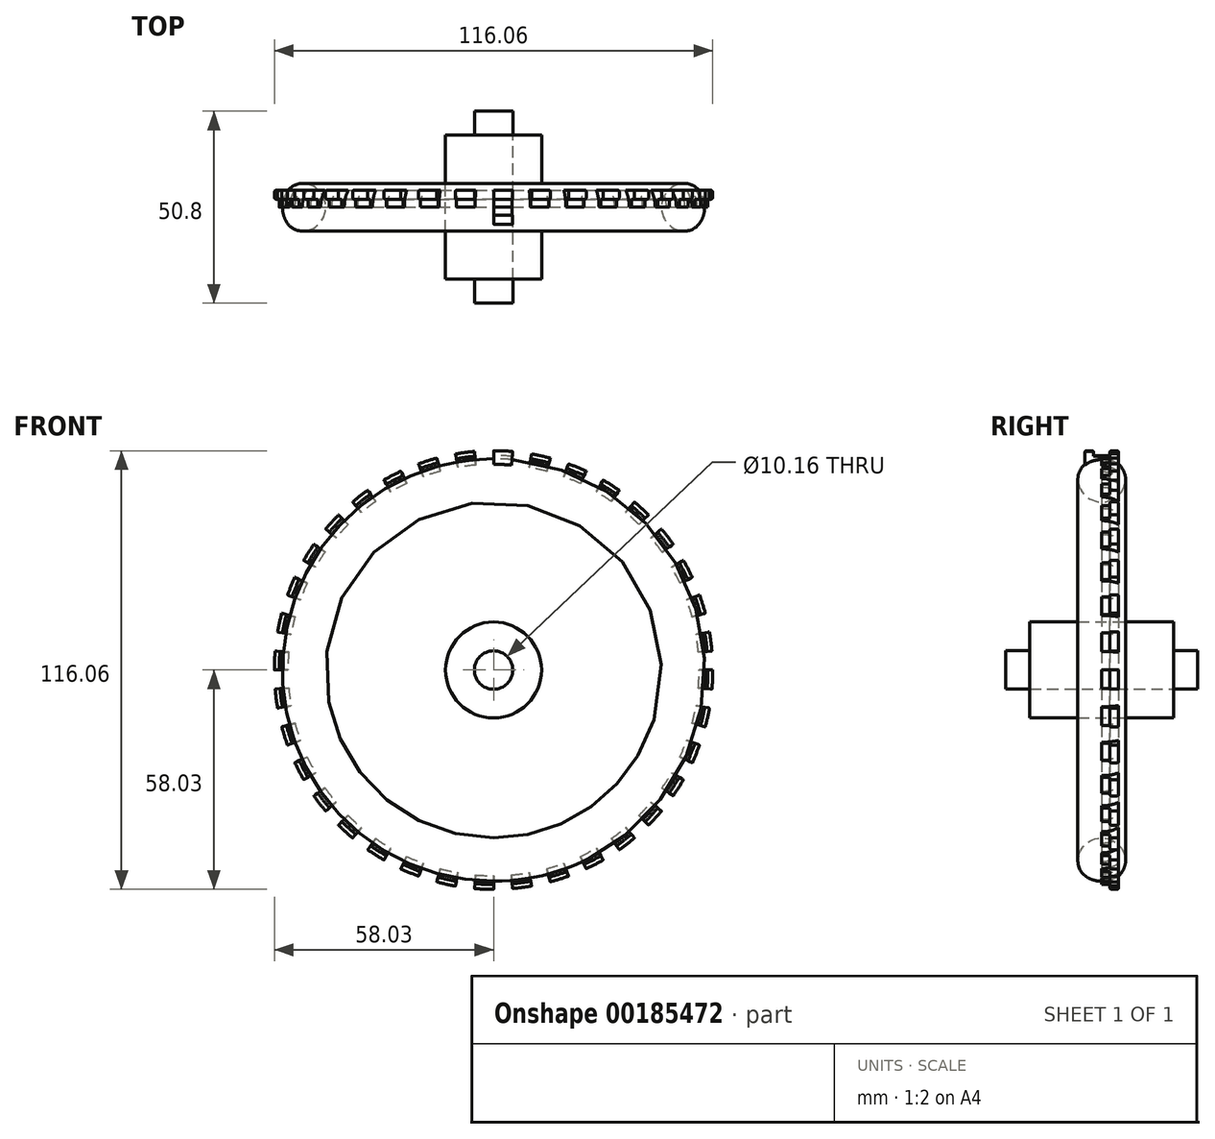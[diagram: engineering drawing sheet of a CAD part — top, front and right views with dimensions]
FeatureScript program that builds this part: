
annotation { "Feature Type Name" : "Feature", "Feature Type Description" : "" }
export const myFeature = defineFeature(function(context is Context, id is Id, definition is map)
    precondition{}
    {
        {
            var Q0;
            Q0=qCreatedBy(makeId("Right.planeOp"),FACE);
            var sketch = newSketch(context, id + "F0", { "sketchPlane" : qUnion([Q0])});
            skArc(sketch, "E0", {"start": v(-5.95, 53.02) * mm, "mid": v(0, 44.45) * mm, "end": v(5.95, 53.02) * mm});
            skLineSegment(sketch, "E1", {"start": v(-27.12, 0) * mm, "end": v(50.11, 0) * mm, "construction": true});
            skArc(sketch, "E2", {"start": v(-5.95, 53.02) * mm, "mid": v(0, 55.88) * mm, "end": v(5.95, 53.02) * mm});
            skSolve(sketch);
        }
        {
            var Q0;
            Q0 = qSketchRegion(id + "F0", true);
            var Q1;
            Q1=sQuery(id+"F0.wireOp",EDGE,"E1");
            revolve(context, id + "F1", {"entities" : qUnion([Q0]), "axis" : qUnion([Q1]), "revolveType" : RevolveType.FULL});
        }
        {
            var Q0;
            {var subQ0=sQuery(id+"F0.wireOp",EDGE,"E2");var subQ1=sQuery(id+"F0.wireOp",EDGE,"E0");Q0=makeQuery(id+"F1.opRevolve","SWEPT_EDGE",EDGE,{"disambiguationData":[OSD([subQ1,subQ0]),TDD([makeQuery(id+"F0.imprint","INTERSECT",VERTEX,{"disambiguationData":[OD(1.0)],"derivedFrom":[subQ1,subQ0]})])]});}
            fillet(context, id + "F2", {"entities" : qUnion([Q0]), "radius" : 5.08 * mm, "tangentPropagation" : true, "allowEdgeOverflow" : false});
        }
        {
            var Q0;
            {var subQ0=sQuery(id+"F0.wireOp",EDGE,"E2");var subQ1=sQuery(id+"F0.wireOp",EDGE,"E0");Q0=makeQuery(id+"F1.opRevolve","SWEPT_EDGE",EDGE,{"disambiguationData":[OSD([subQ1,subQ0]),TDD([makeQuery(id+"F0.imprint","INTERSECT",VERTEX,{"disambiguationData":[OD(0.0)],"derivedFrom":[subQ1,subQ0]})])]});}
            fillet(context, id + "F3", {"entities" : qUnion([Q0]), "radius" : 5.08 * mm, "tangentPropagation" : true, "allowEdgeOverflow" : false});
        }
        {
            var Q0;
            Q0=qCreatedBy(makeId("Right.planeOp"),FACE);
            var sketch = newSketch(context, id + "F4", { "sketchPlane" : qUnion([Q0])});
            skArc(sketch, "E3.0", {"start": v(-4.48, 54.42) * mm, "mid": v(-2.36, 55.5) * mm, "end": v(0, 55.88) * mm});
            skLineSegment(sketch, "E4", {"start": v(-4.48, 54.42) * mm, "end": v(-4.48, 58.03) * mm});
            skLineSegment(sketch, "E5", {"start": v(-4.48, 58.03) * mm, "end": v(-2.14, 58.03) * mm});
            skLineSegment(sketch, "E6", {"start": v(-2.14, 58.03) * mm, "end": v(-2.14, 56.75) * mm});
            skLineSegment(sketch, "E7", {"start": v(-2.14, 56.75) * mm, "end": v(0, 56.75) * mm});
            skLineSegment(sketch, "E8", {"start": v(0, 56.75) * mm, "end": v(0, 55.88) * mm});
            skPoint(sketch, "E9.orphan", {"position": v(-5.95, 53.02) * mm});
            skPoint(sketch, "E10.orphan", {"position": v(5.95, 53.02) * mm});
            skSolve(sketch);
        }
        {
            var Q0;
            Q0 = qSketchRegion(id + "F4", true);
            var Q1;
            Q1=sQuery(id+"F0.wireOp",EDGE,"E1");
            revolve(context, id + "F5", {"entities" : qUnion([Q0]), "axis" : qUnion([Q1]), "revolveType" : RevolveType.ONE_DIRECTION, "angle" : 5 * degree});
        }
        {
            var Q0;
            Q0=makeQuery(id+"F5.opRevolve","SWEPT_EDGE",EDGE,{"disambiguationData":[OSD([sQuery(id+"F4.wireOp",EDGE,"E4"),sQuery(id+"F4.wireOp",EDGE,"E5")])]});
            var Q1;
            Q1=makeQuery(id+"F5.opRevolve","SWEPT_EDGE",EDGE,{"disambiguationData":[OSD([sQuery(id+"F4.wireOp",EDGE,"E5"),sQuery(id+"F4.wireOp",EDGE,"E6")])]});
            fillet(context, id + "F6", {"entities" : qUnion([Q0, Q1]), "radius" : 0.5 * mm, "tangentPropagation" : true, "allowEdgeOverflow" : false});
        }
        {
            var Q0;
            Q0=makeQuery(id+"F5.opRevolve","SWEPT_BODY",BODY,{"disambiguationData":[OSD([sQuery(id+"F4.wireOp",EDGE,"E3.0"),sQuery(id+"F4.wireOp",EDGE,"E4"),sQuery(id+"F4.wireOp",EDGE,"E5"),sQuery(id+"F4.wireOp",EDGE,"E6"),sQuery(id+"F4.wireOp",EDGE,"E7"),sQuery(id+"F4.wireOp",EDGE,"E8")])]});
            var Q1;
            Q1=qCreatedBy(makeId("Front.planeOp"),FACE);
            mirror(context, id + "F7", {"entities" : qUnion([Q0]), "mirrorPlane" : qUnion([Q1])});
        }
        {
            var Q0;
            Q0=makeQuery(id+"F7.opPattern","COPY",BODY,{"derivedFrom":makeQuery(id+"F5.opRevolve","SWEPT_BODY",BODY,{"disambiguationData":[OSD([sQuery(id+"F4.wireOp",EDGE,"E3.0"),sQuery(id+"F4.wireOp",EDGE,"E4"),sQuery(id+"F4.wireOp",EDGE,"E5"),sQuery(id+"F4.wireOp",EDGE,"E6"),sQuery(id+"F4.wireOp",EDGE,"E7"),sQuery(id+"F4.wireOp",EDGE,"E8")])]}),"instanceName":"1"});
            var Q1;
            Q1=sQuery(id+"F0.wireOp",EDGE,"E1");
            circularPattern(context, id + "F8", {"entities" : qUnion([Q0]), "axis" : qUnion([Q1]), "angle" : 10 * degree, "instanceCount" : 36});
        }
        {
            var Q0;
            Q0=qCreatedBy(makeId("Front.planeOp"),FACE);
            var sketch = newSketch(context, id + "F9", { "sketchPlane" : qUnion([Q0])});
            skCircle(sketch, "E11", {"center": v(0, 0) * mm, "radius": 12.7 * mm});
            skCircle(sketch, "E12", {"center": v(0, 0) * mm, "radius": 19.05 * mm});
            skCircle(sketch, "E13", {"center": v(0, 0) * mm, "radius": 5.08 * mm});
            skSolve(sketch);
        }
        {
            var Q0;
            Q0=makeQuery(id+"F9.imprint","IMPRINT",FACE,{"disambiguationData":[TD([[makeQuery(id+"F9.imprint","IMPRINT",EDGE,{"derivedFrom":sQuery(id+"F9.wireOp",EDGE,"E13")}),1.0]])]});
            extrude(context, id + "F10", {"entities" : qUnion([Q0]), "depth" : 25.4 * mm, "hasSecondDirection" : true, "secondDirectionOppositeDirection" : true, "secondDirectionDepth" : 25.4 * mm});
        }
        {
            var Q0;
            Q0=makeQuery(id+"F9.imprint","IMPRINT",FACE,{"disambiguationData":[TD([[makeQuery(id+"F9.imprint","IMPRINT",EDGE,{"derivedFrom":sQuery(id+"F9.wireOp",EDGE,"E11")}),1.0]])]});
            extrude(context, id + "F11", {"entities" : qUnion([Q0]), "depth" : 19.05 * mm, "hasSecondDirection" : true, "secondDirectionOppositeDirection" : true, "secondDirectionDepth" : 19.05 * mm});
        }
    });
